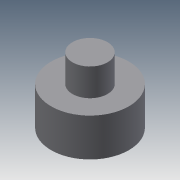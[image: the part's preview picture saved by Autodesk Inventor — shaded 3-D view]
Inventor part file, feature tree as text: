
AUTODESK INVENTOR PART (.ipt)
format: ipt  version: 2013 (Build 170138000, 138)  size: 88,576 bytes
history: native  units: mm
features: sketch x3, extrude x2, plane x1, hole x1
ambient origin geometry x8: Origin, YZ Plane, XZ Plane, XY Plane, X Axis, Y Axis, Z Axis, Center Point
bodies: Solid1 (feature_tree)
feature tree (7):
  extrude  "Extrusion1"  Depth=6.5mm TaperAngle=0.0deg
  plane  "Work Plane1"
  hole  "Hole1"  [1 undecoded]
  extrude  "Extrusion3"  Depth=4.7mm TaperAngle=0.0deg
  sketch  "Sketch1"  dims[d0=13.3mm d1=6.5mm d2=0.0mm]
  sketch  "Sketch3"  dims[d9=2.4mm]
  sketch  "Sketch4"  dims[d10=2.459mm d11=6.65mm d12=4.0mm d13=2.0mm d14=90.0deg d15=6.65mm d16=0.0mm d17=6.0mm d18=4.7mm d19=0.0mm]
note: 1 required parameter value undecoded (feature->parameter linkage not recoverable at this tier; creation-order binding heuristic only, values carry confidence <= 0.55)
